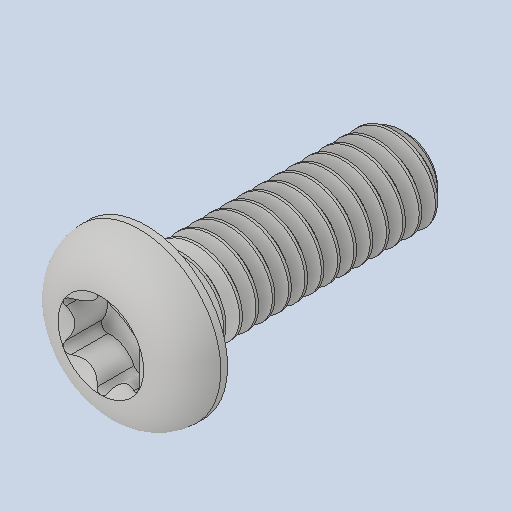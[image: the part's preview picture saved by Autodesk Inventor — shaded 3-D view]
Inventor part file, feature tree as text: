
AUTODESK INVENTOR PART (.ipt)
format: ipt  version: 2023 (Build 270158000, 158)  size: 656,896 bytes
history: native  units: in
note: dims shown in document units (in); Inventor stores cm internally (conversion verified against a paired STEP export)
features: extrude x1
ambient origin geometry x8: Origin, YZ Plane, XZ Plane, XY Plane, X Axis, Y Axis, Z Axis, Center Point
bodies: Solid1 (feature_tree)
feature tree (1):
  extrude  "Extrude16"  [1 undecoded]
note: 1 required parameter value undecoded (feature->parameter linkage not recoverable at this tier; creation-order binding heuristic only, values carry confidence <= 0.55)
